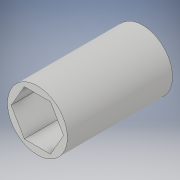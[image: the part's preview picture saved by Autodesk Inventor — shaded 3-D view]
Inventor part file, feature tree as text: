
AUTODESK INVENTOR PART (.ipt)
format: ipt  version: 2018 (Build 220112000, 112)  size: 100,864 bytes
history: native  units: in
note: dims shown in document units (in); Inventor stores cm internally (conversion verified against a paired STEP export)
features: extrude x1, sketch x1
ambient origin geometry x8: Origin, YZ Plane, XZ Plane, XY Plane, X Axis, Y Axis, Z Axis, Center Point
bodies: Solid1 (feature_tree)
feature tree (2):
  extrude  "Extrusion1"  Depth=1.159in
  sketch  "Sketch1"  dims[d0=0.5in d1=0.66in d2=1.159in d3=0.0in]
